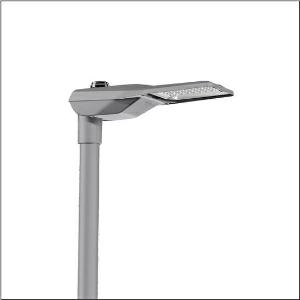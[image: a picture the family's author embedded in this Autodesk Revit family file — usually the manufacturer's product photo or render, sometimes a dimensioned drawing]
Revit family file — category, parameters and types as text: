
# Revit family: streetlight_sl_21_mini___stw1_0a_5xe6e47n08jb_ac66
name_source: partatom
category: Lighting Fixtures
units: mm (PartAtom-declared; Revit-internal decimal feet)

## family parameters
Cut with Voids When Loaded = No
Host = Face
Light Source = No
Part Type = Normal
Room Calculation Point = No
Round Connector Dimension = Use Diameter
Shared = No

## types (1)
- --- (1 x LED, 13390 lm, 87.3 W, 4000K)
    Apparent Load = 87 VA
    CIE Flux Codes = 39 75 98 100 100
    Color Rendering = 70
    Color Temperature = 4000K
    Default Elevation = 1800 mm
    Description = Streetlight SL 21 mini, mast luminaire, primary light control with lens, of PMMA, primary optical cover: cover, of toughened safety glass, transparent, light distribution: STW1.0a, light emission: direct distribution, primary light characteristic: asymmetric, installation type: side-entry, LED, 3G 2.5mm², High Power LED, rated luminous flux: 13.390lm, luminous efficacy: 153lm/W, light colour: 740, colour temperature: 4000K, control: overheat protection, pre-setting: linear dimming characteristic, constant luminous flux control, time-dependent luminous flux control, flexible luminous flux parameterisation, mains connection: 230..240V, AC, 50/60Hz, connection cable pre-assembled, cable length: 10,5m, wiring characteristics: H05VV-F, start of lifetime: 87W, end of service life: 90W, reduction: 40W, luminaire housing, of diecast aluminium (EN AC-44300), powder-coated, Siteco® metallic grey (DB 702S), corrosivity category C5 mid according to DIN EN ISO 12944, multi-level sealing system, sealing non-destructively replaceable, inclination adjustable: 0°, 5°, 10°, 15°, length: 628mm, width: 235mm, height: 110mm, spigot size: 42mm (side-entry), protection rating (complete): IP66, insulation class (complete): insulation class I (protective earthing), certification: CE, ENEC, ENEC+, VDE, impact resistance: IK09, permissible operating ambient temperature for outdoor applications: -40..+50°C, standard-compliant lighting for roads and squares, packaging unit: 1 piece

Light Distribution: STW1.0a
    Height = 110 mm
    Lamp = 1 x LED
    Lamp Light Flux = 13390 lm
    Lamp Power = 87.3 W
    Lamp count = 1
    Length = 625 mm
    Luminous efficacy = 153 lm/W
    Manufacturer = Siteco
    ModVariant = No
    Model = 5XE6E47N08JB
    Number of Poles = 1
    OnlyDefault = Yes
    Power Factor = 1
    Product Name = Streetlight SL 21 mini | STW1.0a
    Product group = mast luminaire | pylon top
    ProductGroupID = 6100
    Protection Class = Protection class I
    Protection Degree = IP 66
    RLX_Detail_Level = 1
    RLX_Emergency_Light_Flux = 0 lm
    RLX_Emergency_Type = 0
    RLX_Emergency_Type_DB = No
    RlxData = <blob elided: 91829 chars, md5=a58fe23a>
    Socket = socket
    Standby Power = 0 W
    System Light Flux = 13390 lm
    System Power = 87 W
    Type Comments = factory setting: luminous flux: 100 % | dim-lin: 254 | 915 mA
    Type Image = l_1294379.jpg
    URL = http://relux.com
    VarID = @adj_104775
    Voltage = 0 V
    Weight = 0.00 kg
    Width = 234 mm

## geometry (parser evidence)
native form markers: Blend x4, Sweep x10
no freeform markers — native parametric forms only
